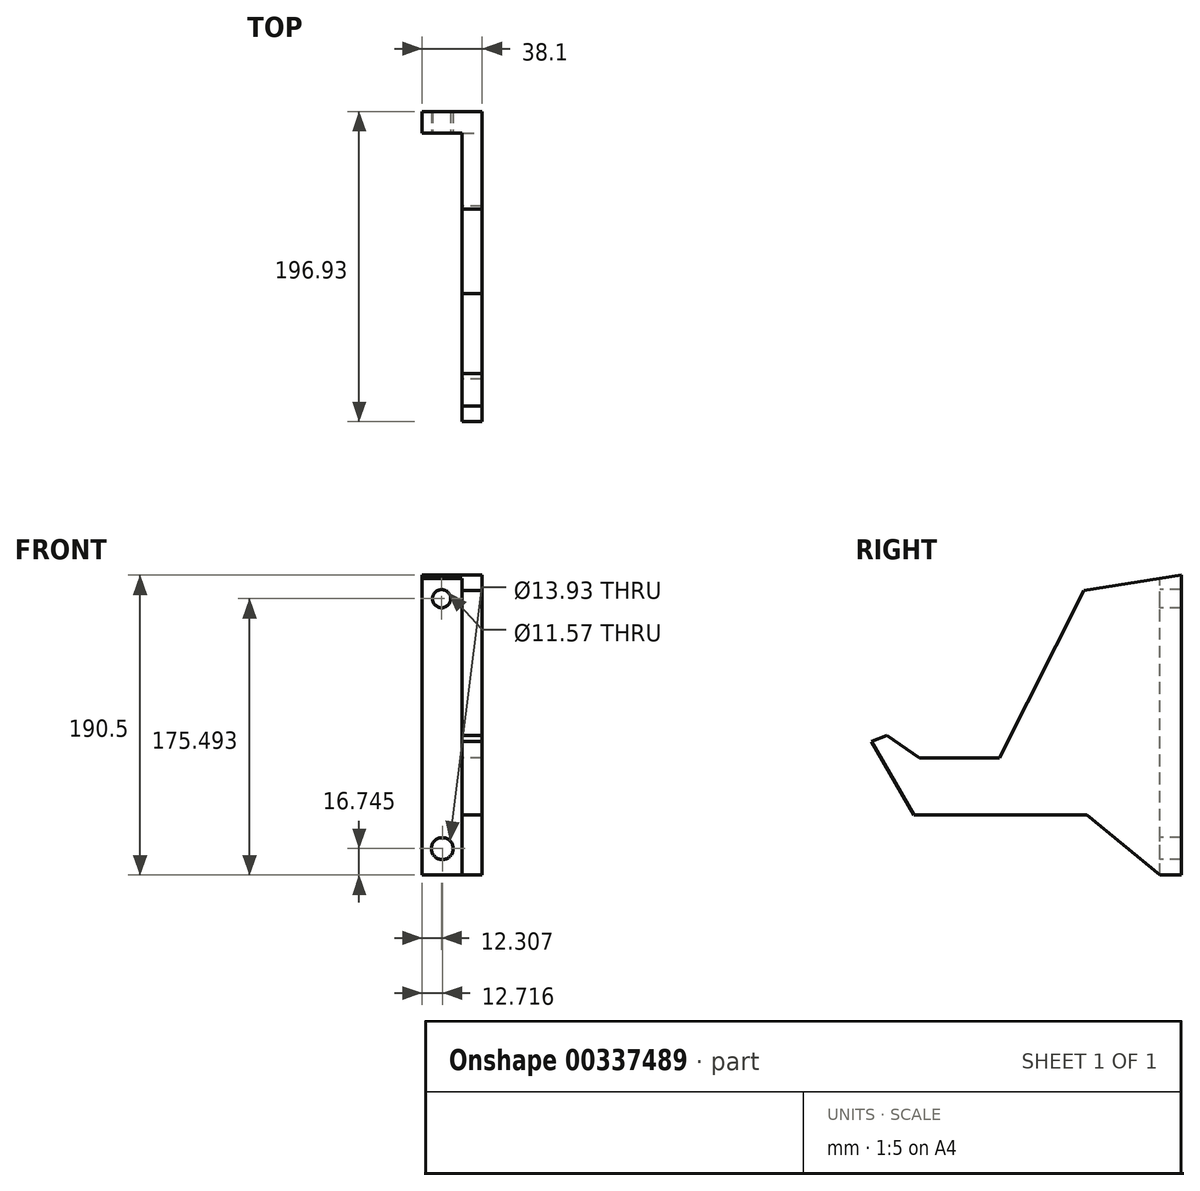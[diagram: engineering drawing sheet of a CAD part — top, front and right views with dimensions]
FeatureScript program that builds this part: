
annotation { "Feature Type Name" : "Feature", "Feature Type Description" : "" }
export const myFeature = defineFeature(function(context is Context, id is Id, definition is map)
    precondition{}
    {
        {
            var Q0;
            Q0=qCreatedBy(makeId("Right.planeOp"),FACE);
            var sketch = newSketch(context, id + "F0", { "sketchPlane" : qUnion([Q0])});
            skLineSegment(sketch, "E0", {"start": v(-82.66, -27.15) * mm, "end": v(87.23, -27.15) * mm});
            skLineSegment(sketch, "E1", {"start": v(87.23, -27.15) * mm, "end": v(87.23, 125.25) * mm});
            skLineSegment(sketch, "E2", {"start": v(87.23, 125.25) * mm, "end": v(25.25, 115.44) * mm});
            skLineSegment(sketch, "E3", {"start": v(25.25, 115.44) * mm, "end": v(-28.36, 9.16) * mm});
            skLineSegment(sketch, "E4", {"start": v(-28.36, 9.16) * mm, "end": v(-79.16, 9.16) * mm});
            skLineSegment(sketch, "E5", {"start": v(-79.16, 9.16) * mm, "end": v(-99.85, 23.26) * mm});
            skLineSegment(sketch, "E6", {"start": v(-99.85, 23.26) * mm, "end": v(-109.7, 19.62) * mm});
            skLineSegment(sketch, "E7", {"start": v(-109.7, 19.62) * mm, "end": v(-82.66, -27.15) * mm});
            skSolve(sketch);
        }
        {
            var Q0;
            Q0=makeQuery(id+"F0.imprint","IMPRINT",FACE,{"disambiguationData":[TD([[makeQuery(id+"F0.imprint","IMPRINT",EDGE,{"derivedFrom":sQuery(id+"F0.wireOp",EDGE,"E0")}),1.0]])]});
            extrude(context, id + "F1", {"entities" : qUnion([Q0]), "depth" : 12.7 * mm});
        }
        {
            var Q0;
            Q0=makeQuery(id+"F1.opExtrude","SWEPT_FACE",FACE,{"disambiguationData":[OSD([sQuery(id+"F0.wireOp",EDGE,"E0")])]});
            var sketch = newSketch(context, id + "F2", { "sketchPlane" : qUnion([Q0])});
            skLineSegment(sketch, "E8", {"start": v(0, -87.23) * mm, "end": v(12.7, -87.23) * mm});
            skLineSegment(sketch, "E9", {"start": v(12.7, -87.23) * mm, "end": v(12.7, -27.27) * mm});
            skLineSegment(sketch, "E10", {"start": v(12.7, -27.27) * mm, "end": v(0, -27.27) * mm});
            skLineSegment(sketch, "E11", {"start": v(0, -27.27) * mm, "end": v(0, -87.23) * mm});
            skSolve(sketch);
        }
        {
            var Q0;
            Q0=makeQuery(id+"F2.imprint","IMPRINT",FACE,{"disambiguationData":[TD([[makeQuery(id+"F2.imprint","IMPRINT",EDGE,{"derivedFrom":sQuery(id+"F2.wireOp",EDGE,"E8")}),-1.0]])]});
            extrude(context, id + "F3", {"entities" : qUnion([Q0]), "operationType" : NewBodyOperationType.ADD, "depth" : 38.1 * mm});
        }
        {
            var Q0;
            Q0=makeQuery(id+"F3.boolean.opBoolean","MERGE",FACE,{"derivedFrom":[makeQuery(id+"F1.opExtrude","CAP_FACE",FACE,{"disambiguationData":[OSD([sQuery(id+"F0.wireOp",EDGE,"E0"),sQuery(id+"F0.wireOp",EDGE,"E1"),sQuery(id+"F0.wireOp",EDGE,"E2"),sQuery(id+"F0.wireOp",EDGE,"E3"),sQuery(id+"F0.wireOp",EDGE,"E4"),sQuery(id+"F0.wireOp",EDGE,"E5"),sQuery(id+"F0.wireOp",EDGE,"E6"),sQuery(id+"F0.wireOp",EDGE,"E7")])],"isStart":false}),makeQuery(id+"F3.opExtrude","SWEPT_FACE",FACE,{"disambiguationData":[OSD([sQuery(id+"F2.wireOp",EDGE,"E9")])]})]});
            var sketch = newSketch(context, id + "F4", { "sketchPlane" : qUnion([Q0])});
            skLineSegment(sketch, "E12", {"start": v(27.27, -27.15) * mm, "end": v(73.6, -65.25) * mm});
            skLineSegment(sketch, "E13", {"start": v(73.6, -65.25) * mm, "end": v(27.27, -65.25) * mm});
            skLineSegment(sketch, "E14", {"start": v(27.27, -65.25) * mm, "end": v(27.27, -27.15) * mm});
            skSolve(sketch);
        }
        {
            var Q0;
            Q0=makeQuery(id+"F4.imprint","IMPRINT",FACE,{"disambiguationData":[TD([[makeQuery(id+"F4.imprint","IMPRINT",EDGE,{"derivedFrom":sQuery(id+"F4.wireOp",EDGE,"E12")}),-1.0]])]});
            extrude(context, id + "F5", {"entities" : qUnion([Q0]), "operationType" : NewBodyOperationType.REMOVE, "oppositeDirection" : true, "depth" : 25.4 * mm});
        }
        {
            var Q0;
            Q0=makeQuery(id+"F3.boolean.opBoolean","MERGE",FACE,{"derivedFrom":[makeQuery(id+"F1.opExtrude","CAP_FACE",FACE,{"disambiguationData":[OSD([sQuery(id+"F0.wireOp",EDGE,"E0"),sQuery(id+"F0.wireOp",EDGE,"E1"),sQuery(id+"F0.wireOp",EDGE,"E2"),sQuery(id+"F0.wireOp",EDGE,"E3"),sQuery(id+"F0.wireOp",EDGE,"E4"),sQuery(id+"F0.wireOp",EDGE,"E5"),sQuery(id+"F0.wireOp",EDGE,"E6"),sQuery(id+"F0.wireOp",EDGE,"E7")])],"isStart":true}),makeQuery(id+"F3.opExtrude","SWEPT_FACE",FACE,{"disambiguationData":[OSD([sQuery(id+"F2.wireOp",EDGE,"E11")])]})]});
            var sketch = newSketch(context, id + "F6", { "sketchPlane" : qUnion([Q0])});
            skLineSegment(sketch, "E15", {"start": v(-87.23, -65.25) * mm, "end": v(-73.6, -65.25) * mm});
            skLineSegment(sketch, "E16", {"start": v(-73.6, -65.25) * mm, "end": v(-73.6, 123.1) * mm});
            skLineSegment(sketch, "E17", {"start": v(-73.6, 123.1) * mm, "end": v(-87.23, 125.25) * mm});
            skLineSegment(sketch, "E18", {"start": v(-87.23, 125.25) * mm, "end": v(-87.23, -65.25) * mm});
            skSolve(sketch);
        }
        {
            var Q0;
            Q0=makeQuery(id+"F6.imprint","IMPRINT",FACE,{"disambiguationData":[TD([[makeQuery(id+"F6.imprint","IMPRINT",EDGE,{"derivedFrom":sQuery(id+"F6.wireOp",EDGE,"E15")}),-1.0]])]});
            extrude(context, id + "F7", {"entities" : qUnion([Q0]), "operationType" : NewBodyOperationType.ADD, "depth" : 25.4 * mm});
        }
        {
            var Q0;
            Q0=makeQuery(id+"F7.opExtrude","SWEPT_FACE",FACE,{"disambiguationData":[OSD([sQuery(id+"F6.wireOp",EDGE,"E16")])]});
            var sketch = newSketch(context, id + "F8", { "sketchPlane" : qUnion([Q0])});
            skCircle(sketch, "E19", {"center": v(-13.1, 110.24) * mm, "radius": 5.79 * mm});
            skCircle(sketch, "E20", {"center": v(-12.68, -48.5) * mm, "radius": 6.97 * mm});
            skSolve(sketch);
        }
        {
            var Q0;
            Q0=makeQuery(id+"F8.imprint","IMPRINT",FACE,{"disambiguationData":[TD([[makeQuery(id+"F8.imprint","IMPRINT",EDGE,{"derivedFrom":sQuery(id+"F8.wireOp",EDGE,"E19")}),1.0]])]});
            var Q1;
            Q1=makeQuery(id+"F8.imprint","IMPRINT",FACE,{"disambiguationData":[TD([[makeQuery(id+"F8.imprint","IMPRINT",EDGE,{"derivedFrom":sQuery(id+"F8.wireOp",EDGE,"E20")}),1.0]])]});
            extrude(context, id + "F9", {"entities" : qUnion([Q0, Q1]), "operationType" : NewBodyOperationType.REMOVE, "oppositeDirection" : true, "depth" : 25.4 * mm});
        }
    });
